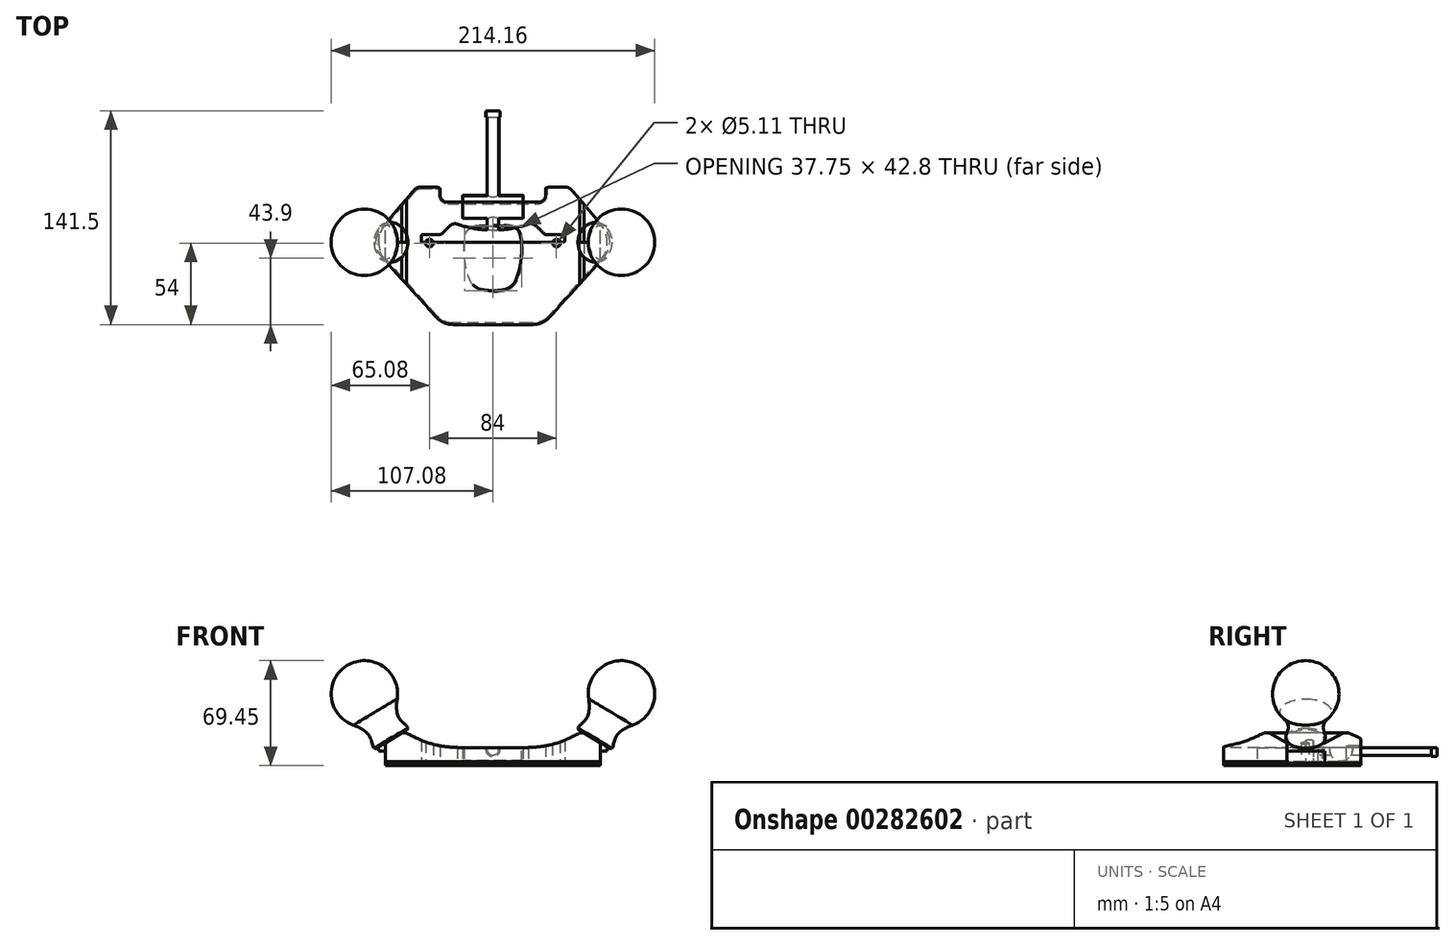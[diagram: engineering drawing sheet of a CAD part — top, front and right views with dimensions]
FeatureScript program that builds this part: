
annotation { "Feature Type Name" : "Feature", "Feature Type Description" : "" }
export const myFeature = defineFeature(function(context is Context, id is Id, definition is map)
    precondition{}
    {
        {
            var Q0;
            Q0=qCreatedBy(makeId("Top.planeOp"),FACE);
            var sketch = newSketch(context, id + "F0", { "sketchPlane" : qUnion([Q0])});
            skLineSegment(sketch, "E0", {"start": v(-47.5, 0) * mm, "end": v(47.5, 0) * mm});
            skPoint(sketch, "E1", {"position": v(0, 0) * mm});
            skLineSegment(sketch, "E2", {"start": v(47.5, 0) * mm, "end": v(47.5, 5) * mm});
            skLineSegment(sketch, "E3", {"start": v(47.5, 5) * mm, "end": v(35.5, 5) * mm});
            skFitSpline(sketch, "E4", {"points": [v(35.5, 5) * mm, v(23.5, 12) * mm], "startDerivative": vector(-8.93, 0) * mm, "endDerivative": vector(-15.16, -5.98) * mm});
            skFitSpline(sketch, "E5.MirrorCS", {"points": [v(-35.5, 5) * mm, v(-23.5, 12) * mm], "startDerivative": vector(8.93, 0) * mm, "endDerivative": vector(15.16, -5.98) * mm});
            skLineSegment(sketch, "E6.MirrorCS", {"start": v(-47.5, 5) * mm, "end": v(-35.5, 5) * mm});
            skLineSegment(sketch, "E7.MirrorCS", {"start": v(-47.5, 0) * mm, "end": v(-47.5, 5) * mm});
            skArc(sketch, "E8", {"start": v(-23.5, 12) * mm, "mid": v(0, 8) * mm, "end": v(23.5, 12) * mm});
            skPoint(sketch, "E9", {"position": v(0, 8) * mm});
            skSolve(sketch);
        }
        {
            var Q0;
            Q0=makeQuery(id+"F0.imprint","IMPRINT",FACE,{"disambiguationData":[TD([[makeQuery(id+"F0.imprint","IMPRINT",EDGE,{"derivedFrom":sQuery(id+"F0.wireOp",EDGE,"E0")}),1.0]])]});
            extrude(context, id + "F1", {"entities" : qUnion([Q0]), "depth" : 18.5 * mm});
        }
        {
            var Q0;
            Q0=makeQuery(id+"F1.opExtrude","SWEPT_FACE",FACE,{"disambiguationData":[OSD([sQuery(id+"F0.wireOp",EDGE,"E0")])]});
            var sketch = newSketch(context, id + "F2", { "sketchPlane" : qUnion([Q0])});
            skCircle(sketch, "E10", {"center": v(0, 9.25) * mm, "radius": 3.95 * mm});
            skCircle(sketch, "E11", {"center": v(0, 9.25) * mm, "radius": 4.75 * mm});
            skSolve(sketch);
        }
        {
            var Q0;
            Q0=makeQuery(id+"F2.imprint","IMPRINT",FACE,{"disambiguationData":[TD([[makeQuery(id+"F2.imprint","IMPRINT",EDGE,{"derivedFrom":sQuery(id+"F2.wireOp",EDGE,"E10")}),1.0]])]});
            extrude(context, id + "F3", {"entities" : qUnion([Q0]), "operationType" : NewBodyOperationType.ADD, "oppositeDirection" : true, "depth" : 87 * mm});
        }
        {
            var Q0;
            Q0=makeQuery(id+"F2.imprint","IMPRINT",FACE,{"disambiguationData":[TD([[makeQuery(id+"F2.imprint","IMPRINT",EDGE,{"derivedFrom":sQuery(id+"F2.wireOp",EDGE,"E10")}),-1.0]])]});
            var Q1;
            Q1=makeQuery(id+"F3.opExtrude","CAP_FACE",FACE,{"disambiguationData":[OSD([sQuery(id+"F2.wireOp",EDGE,"E10")])],"isStart":false});
            extrude(context, id + "F4", {"entities" : qUnion([Q0]), "operationType" : NewBodyOperationType.ADD, "endBound" : BoundingType.UP_TO_SURFACE, "oppositeDirection" : true, "endBoundEntityFace" : qUnion([Q1]), "depth" : 25 * mm, "hasSecondDirection" : true, "secondDirectionOppositeDirection" : true, "secondDirectionDepth" : 83 * mm});
        }
        {
            var Q0;
            Q0=qCreatedBy(makeId("Right.planeOp"),FACE);
            var sketch = newSketch(context, id + "F5", { "sketchPlane" : qUnion([Q0])});
            skPoint(sketch, "E12.0", {"position": v(0, 9.25) * mm});
            skCircle(sketch, "E13", {"center": v(23.3, 9.25) * mm, "radius": 7.65 * mm});
            skSolve(sketch);
        }
        {
            var Q0;
            Q0=makeQuery(id+"F5.imprint","IMPRINT",FACE,{"disambiguationData":[TD([[makeQuery(id+"F5.imprint","IMPRINT",EDGE,{"derivedFrom":sQuery(id+"F5.wireOp",EDGE,"E13")}),1.0]])]});
            extrude(context, id + "F6", {"entities" : qUnion([Q0]), "operationType" : NewBodyOperationType.ADD, "endBound" : BoundingType.SYMMETRIC, "depth" : 40 * mm});
        }
        {
            var Q0;
            Q0=makeQuery(id+"F1.opExtrude","SWEPT_EDGE",EDGE,{"disambiguationData":[OSD([sQuery(id+"F0.wireOp",EDGE,"E0"),sQuery(id+"F0.wireOp",EDGE,"E7.MirrorCS")])]});
            var Q1;
            Q1=makeQuery(id+"F1.opExtrude","SWEPT_EDGE",EDGE,{"disambiguationData":[OSD([sQuery(id+"F0.wireOp",EDGE,"E6.MirrorCS"),sQuery(id+"F0.wireOp",EDGE,"E7.MirrorCS")])]});
            var Q2;
            Q2=makeQuery(id+"F1.opExtrude","SWEPT_EDGE",EDGE,{"disambiguationData":[OSD([sQuery(id+"F0.wireOp",EDGE,"E0"),sQuery(id+"F0.wireOp",EDGE,"E2")])]});
            var Q3;
            Q3=makeQuery(id+"F1.opExtrude","SWEPT_EDGE",EDGE,{"disambiguationData":[OSD([sQuery(id+"F0.wireOp",EDGE,"E2"),sQuery(id+"F0.wireOp",EDGE,"E3")])]});
            var Q4;
            Q4=makeQuery(id+"F4.opExtrude","CAP_EDGE",EDGE,{"disambiguationData":[OSD([sQuery(id+"F2.wireOp",EDGE,"E11")])],"isStart":false});
            fillet(context, id + "F7", {"entities" : qUnion([Q0, Q1, Q2, Q3, Q4]), "radius" : 1 * mm, "tangentPropagation" : true, "allowEdgeOverflow" : false});
        }
        {
            var Q0;
            Q0=qCreatedBy(makeId("Top.planeOp"),FACE);
            var sketch = newSketch(context, id + "F8", { "sketchPlane" : qUnion([Q0])});
            skLineSegment(sketch, "E14", {"start": v(-25, -54.5) * mm, "end": v(25, -54.5) * mm});
            skPoint(sketch, "E15", {"position": v(0, -54.5) * mm});
            skLineSegment(sketch, "E16", {"start": v(37.5, -49.5) * mm, "end": v(71, -12.5) * mm});
            skLineSegment(sketch, "E17", {"start": v(71, -12.5) * mm, "end": v(71, 12.5) * mm});
            skPoint(sketch, "E18", {"position": v(71, 0) * mm});
            skFitSpline(sketch, "E19", {"points": [v(25, -54.5) * mm, v(37.5, -49.5) * mm], "startDerivative": vector(17.7, 0) * mm, "endDerivative": vector(9.15, 10.1) * mm});
            skLineSegment(sketch, "E20", {"start": v(71, 12.5) * mm, "end": v(53, 33.5) * mm});
            skLineSegment(sketch, "E21", {"start": v(47.5, 36.5) * mm, "end": v(38, 36.5) * mm});
            skPoint(sketch, "E22", {"position": v(0, 36.5) * mm});
            skLineSegment(sketch, "E23", {"start": v(-35, 26.5) * mm, "end": v(30, 26.5) * mm});
            skPoint(sketch, "E24", {"position": v(0, 26.5) * mm});
            skFitSpline(sketch, "E25", {"points": [v(47.5, 36.5) * mm, v(53, 33.5) * mm], "startDerivative": vector(8.49, 0) * mm, "endDerivative": vector(5.57, -6.5) * mm});
            skLineSegment(sketch, "E26", {"start": v(35, 31.5) * mm, "end": v(35, 35.69) * mm});
            skLineSegment(sketch, "E27", {"start": v(38, 36.5) * mm, "end": v(47.5, 36.5) * mm});
            skPoint(sketch, "E28.visualSharp", {"position": v(35, 26.5) * mm});
            skArc(sketch, "E28.filletArc", {"start": v(30, 26.5) * mm, "mid": v(33.54, 27.96) * mm, "end": v(35, 31.5) * mm});
            skFitSpline(sketch, "E29", {"points": [v(38, 36.5) * mm, v(33, 31.5) * mm], "startDerivative": vector(-10.17, 0) * mm, "endDerivative": vector(0, -8.22) * mm});
            skFitSpline(sketch, "E30", {"points": [v(38, 36.5) * mm, v(33, 31.5) * mm], "startDerivative": vector(-10.17, 0) * mm, "endDerivative": vector(0, -8.22) * mm, "construction": true});
            skLineSegment(sketch, "E31.trimOffspring", {"start": v(35, 36.5) * mm, "end": v(-47.5, 36.5) * mm, "construction": true});
            skFitSpline(sketch, "E32.MirrorCS", {"points": [v(-25, -54.5) * mm, v(-37.5, -49.5) * mm], "startDerivative": vector(-17.7, 0) * mm, "endDerivative": vector(-9.15, 10.1) * mm});
            skLineSegment(sketch, "E33.MirrorCS", {"start": v(-37.5, -49.5) * mm, "end": v(-71, -12.5) * mm});
            skLineSegment(sketch, "E34.MirrorCS", {"start": v(-71, -12.5) * mm, "end": v(-71, 12.5) * mm});
            skLineSegment(sketch, "E35.MirrorCS", {"start": v(-71, 12.5) * mm, "end": v(-53, 33.5) * mm});
            skFitSpline(sketch, "E36.MirrorCS", {"points": [v(-47.5, 36.5) * mm, v(-53, 33.5) * mm], "startDerivative": vector(-8.49, 0) * mm, "endDerivative": vector(-5.57, -6.5) * mm});
            skLineSegment(sketch, "E37.MirrorCS", {"start": v(-47.5, 36.5) * mm, "end": v(-38, 36.5) * mm, "construction": true});
            skLineSegment(sketch, "E38.MirrorCS", {"start": v(-47.5, 36.5) * mm, "end": v(-38, 36.5) * mm});
            skFitSpline(sketch, "E39.MirrorCS", {"points": [v(-38, 36.5) * mm, v(-33, 31.5) * mm], "startDerivative": vector(10.17, 0) * mm, "endDerivative": vector(0, -8.22) * mm});
            skLineSegment(sketch, "E40.MirrorCS", {"start": v(-35, 31.5) * mm, "end": v(-35, 35.69) * mm});
            skArc(sketch, "E41.MirrorCS", {"start": v(-30, 26.5) * mm, "mid": v(-33.54, 27.96) * mm, "end": v(-35, 31.5) * mm});
            skFitSpline(sketch, "E42", {"points": [v(0, -32) * mm, v(16, -23.23) * mm, v(18, 5.38) * mm, v(0, 10.8) * mm], "startDerivative": vector(99.32, 0) * mm, "endDerivative": vector(-122.6, 0) * mm});
            skFitSpline(sketch, "E43.MirrorCS", {"points": [v(0, -32) * mm, v(-16, -23.23) * mm, v(-18, 5.38) * mm, v(0, 10.8) * mm], "startDerivative": vector(-99.32, 0) * mm, "endDerivative": vector(122.6, 0) * mm});
            skPoint(sketch, "E44", {"position": v(42, -0.5) * mm});
            skArc(sketch, "E45", {"start": v(71, -12.5) * mm, "mid": v(75.62, 0) * mm, "end": v(71, 12.5) * mm});
            skArc(sketch, "E46.MirrorCS", {"start": v(-71, -12.5) * mm, "mid": v(-75.62, 0) * mm, "end": v(-71, 12.5) * mm});
            skPoint(sketch, "E47.MirrorP", {"position": v(-42, -0.5) * mm});
            skSolve(sketch);
        }
        {
            var Q0;
            Q0=makeQuery(id+"F8.imprint","IMPRINT",FACE,{"disambiguationData":[TD([[makeQuery(id+"F8.imprint","IMPRINT",EDGE,{"derivedFrom":sQuery(id+"F8.wireOp",EDGE,"E14")}),1.0]])]});
            var Q1;
            Q1=makeQuery(id+"F8.imprint","IMPRINT",FACE,{"disambiguationData":[TD([[makeQuery(id+"F8.imprint","IMPRINT",EDGE,{"derivedFrom":sQuery(id+"F8.wireOp",EDGE,"E17")}),-1.0]])]});
            var Q2;
            Q2=makeQuery(id+"F8.imprint","IMPRINT",FACE,{"disambiguationData":[TD([[makeQuery(id+"F8.imprint","IMPRINT",EDGE,{"derivedFrom":sQuery(id+"F8.wireOp",EDGE,"E34.MirrorCS")}),1.0]])]});
            extrude(context, id + "F9", {"entities" : qUnion([Q0, Q1, Q2]), "depth" : 20 * mm});
        }
        {
            var Q0;
            Q0=makeQuery(id+"F8.imprint","IMPRINT",FACE,{"disambiguationData":[TD([[makeQuery(id+"F8.imprint","IMPRINT",EDGE,{"derivedFrom":sQuery(id+"F8.wireOp",EDGE,"E34.MirrorCS")}),1.0]])]});
            var Q1;
            Q1=makeQuery(id+"F8.imprint","IMPRINT",FACE,{"disambiguationData":[TD([[makeQuery(id+"F8.imprint","IMPRINT",EDGE,{"derivedFrom":sQuery(id+"F8.wireOp",EDGE,"E17")}),-1.0]])]});
            extrude(context, id + "F10", {"entities" : qUnion([Q0, Q1]), "operationType" : NewBodyOperationType.REMOVE, "depth" : 8 * mm});
        }
        {
            var Q0;
            Q0=qCreatedBy(makeId("Front.planeOp"),FACE);
            var sketch = newSketch(context, id + "F11", { "sketchPlane" : qUnion([Q0])});
            skLineSegment(sketch, "E48", {"start": v(-20, 10.4) * mm, "end": v(20, 10.4) * mm});
            skPoint(sketch, "E49", {"position": v(0, 10.4) * mm});
            skFitSpline(sketch, "E50", {"points": [v(20, 10.4) * mm, v(57.32, 20) * mm], "startDerivative": vector(50.84, 0) * mm, "endDerivative": vector(35.71, 18.47) * mm});
            skLineSegment(sketch, "E51", {"start": v(75.62, 10.8) * mm, "end": v(60.31, 20) * mm});
            skLineSegment(sketch, "E52", {"start": v(0, 0) * mm, "end": v(75.62, 0) * mm});
            skPoint(sketch, "E53.0", {"position": v(75.62, 20) * mm});
            skLineSegment(sketch, "E54", {"start": v(75.62, 10.8) * mm, "end": v(75.62, 8) * mm});
            skLineSegment(sketch, "E55", {"start": v(75.62, 8) * mm, "end": v(75.62, 0) * mm});
            skLineSegment(sketch, "E56", {"start": v(57.32, 20) * mm, "end": v(60.31, 20) * mm});
            skFitSpline(sketch, "E57.MirrorCS", {"points": [v(-20, 10.4) * mm, v(-57.32, 20) * mm], "startDerivative": vector(-50.84, 0) * mm, "endDerivative": vector(-35.71, 18.47) * mm});
            skLineSegment(sketch, "E58.MirrorCS", {"start": v(-57.32, 20) * mm, "end": v(-60.31, 20) * mm});
            skLineSegment(sketch, "E59.MirrorCS", {"start": v(-75.62, 10.8) * mm, "end": v(-60.31, 20) * mm});
            skLineSegment(sketch, "E60.MirrorCS", {"start": v(-75.62, 10.8) * mm, "end": v(-75.62, 8) * mm});
            skLineSegment(sketch, "E61.MirrorCS", {"start": v(-75.62, 8) * mm, "end": v(-75.62, 0) * mm});
            skLineSegment(sketch, "E62.MirrorCS", {"start": v(0, 0) * mm, "end": v(-75.62, 0) * mm});
            skPoint(sketch, "E63", {"position": v(67.05, 15.95) * mm});
            skLineSegment(sketch, "E64", {"start": v(67.05, 15.95) * mm, "end": v(96.4, 64.8) * mm});
            skLineSegment(sketch, "E65", {"start": v(67.05, 15.95) * mm, "end": v(78.02, 9.36) * mm});
            skArc(sketch, "E66", {"start": v(73.75, 27.1) * mm, "mid": v(82.9, 24.06) * mm, "end": v(92.48, 25.23) * mm, "construction": true});
            skFitSpline(sketch, "E67", {"points": [v(92.48, 25.23) * mm, v(78.02, 9.36) * mm], "startDerivative": vector(-46.63, -16.14) * mm, "endDerivative": vector(-11.75, -8.8) * mm});
            skArc(sketch, "E68", {"start": v(92.48, 25.23) * mm, "mid": v(106.97, 43.78) * mm, "end": v(96.4, 64.8) * mm});
            skSolve(sketch);
        }
        {
            var Q0;
            {var subQ0=sQuery(id+"F11.wireOp",EDGE,"E58.MirrorCS");Q0=makeQuery(id+"F11.imprint","IMPRINT",FACE,{"disambiguationData":[TD([[makeQuery(id+"F11.imprint","IMPRINT",EDGE,{"derivedFrom":subQ0}),1.0]])]});}
            var Q1;
            {var subQ1=sQuery(id+"F11.wireOp",EDGE,"E48");Q1=makeQuery(id+"F11.imprint","IMPRINT",FACE,{"disambiguationData":[TD([[makeQuery(id+"F11.imprint","IMPRINT",EDGE,{"derivedFrom":subQ1}),-1.0]])]});}
            var Q2;
            Q2=makeQuery(id+"F11.imprint","IMPRINT",FACE,{"disambiguationData":[TD([[makeQuery(id+"F11.imprint","IMPRINT",EDGE,{"derivedFrom":sQuery(id+"F11.wireOp",EDGE,"E51")}),1.0]])]});
            extrude(context, id + "F12", {"entities" : qUnion([Q0, Q1, Q2]), "operationType" : NewBodyOperationType.INTERSECT, "endBound" : BoundingType.THROUGH_ALL, "oppositeDirection" : true, "depth" : 25 * mm, "hasSecondDirection" : true, "secondDirectionBound" : SecondDirectionBoundingType.THROUGH_ALL, "secondDirectionOppositeDirection" : false, "secondDirectionDepth" : 25 * mm});
        }
        {
            var Q0;
            {var subQ3=sQuery(id+"F11.wireOp",EDGE,"E64");Q0=makeQuery(id+"F11.imprint","IMPRINT",FACE,{"disambiguationData":[TD([[makeQuery(id+"F11.imprint","IMPRINT",EDGE,{"derivedFrom":subQ3}),-1.0]])]});}
            var Q1;
            Q1=sQuery(id+"F11.wireOp",EDGE,"E64");
            revolve(context, id + "F13", {"entities" : qUnion([Q0]), "axis" : qUnion([Q1]), "revolveType" : RevolveType.FULL});
        }
        {
            var Q0;
            Q0=makeQuery(id+"F13.opRevolve","SWEPT_EDGE",EDGE,{"disambiguationData":[OSD([sQuery(id+"F11.wireOp",EDGE,"E65"),sQuery(id+"F11.wireOp",EDGE,"E67")])]});
            chamfer(context, id + "F14", {"entities" : qUnion([Q0]), "width" : 1 * mm, "tangentPropagation" : true});
        }
        {
            var Q0;
            Q0=makeQuery(id+"F13.opRevolve","SWEPT_BODY",BODY,{"disambiguationData":[OSD([sQuery(id+"F11.wireOp",EDGE,"E64"),sQuery(id+"F11.wireOp",EDGE,"E65"),sQuery(id+"F11.wireOp",EDGE,"E67"),sQuery(id+"F11.wireOp",EDGE,"E68")])]});
            var Q1;
            Q1=qCreatedBy(makeId("Right.planeOp"),FACE);
            mirror(context, id + "F15", {"entities" : qUnion([Q0]), "mirrorPlane" : qUnion([Q1])});
        }
        {
            var Q0;
            Q0=sQuery(id+"F8.wireOp",VERTEX,"E47.MirrorP");
            var Q1;
            Q1=sQuery(id+"F8.wireOp",VERTEX,"E44");
            var Q2;
            Q2=makeQuery(id+"F9.opExtrude","SWEPT_BODY",BODY,{"disambiguationData":[OSD([sQuery(id+"F8.wireOp",EDGE,"E14"),sQuery(id+"F8.wireOp",EDGE,"E16"),sQuery(id+"F8.wireOp",EDGE,"E19"),sQuery(id+"F8.wireOp",EDGE,"E20"),sQuery(id+"F8.wireOp",EDGE,"E23"),sQuery(id+"F8.wireOp",EDGE,"E25"),sQuery(id+"F8.wireOp",EDGE,"E26"),sQuery(id+"F8.wireOp",EDGE,"E27"),sQuery(id+"F8.wireOp",EDGE,"E28.filletArc"),sQuery(id+"F8.wireOp",EDGE,"E29"),sQuery(id+"F8.wireOp",EDGE,"E32.MirrorCS"),sQuery(id+"F8.wireOp",EDGE,"E33.MirrorCS"),sQuery(id+"F8.wireOp",EDGE,"E35.MirrorCS"),sQuery(id+"F8.wireOp",EDGE,"E36.MirrorCS"),sQuery(id+"F8.wireOp",EDGE,"E38.MirrorCS"),sQuery(id+"F8.wireOp",EDGE,"E39.MirrorCS"),sQuery(id+"F8.wireOp",EDGE,"E40.MirrorCS"),sQuery(id+"F8.wireOp",EDGE,"E41.MirrorCS"),sQuery(id+"F8.wireOp",EDGE,"E42"),sQuery(id+"F8.wireOp",EDGE,"E43.MirrorCS"),sQuery(id+"F8.wireOp",EDGE,"E45"),sQuery(id+"F8.wireOp",EDGE,"E46.MirrorCS")])]});
            hole(context, id + "F16", {"style" : HoleStyle.SIMPLE, "endStyle" : HoleEndStyle.THROUGH, "oppositeDirection" : true, "standardTappedOrClearance" : lookupTablePath({ "standard" : "ANSI", "fit" : "Normal (ASME)", "size" : "#10", "type" : "Clearance" }), "standardBlindInLast" : lookupTablePath({ "fit" : "Free", "standard" : "ANSI", "size" : "#10", "type" : "Clearance" }), "holeDiameter" : 5.1 * mm, "tappedDepth" : 12 * mm, "tapClearance" : 3, "locations" : qUnion([Q0, Q1]), "scope" : qUnion([Q2])});
        }
        {
            var Q0;
            Q0=makeQuery(id+"F8.imprint","IMPRINT",FACE,{"disambiguationData":[TD([[makeQuery(id+"F8.imprint","IMPRINT",EDGE,{"derivedFrom":sQuery(id+"F8.wireOp",EDGE,"E14")}),1.0]])]});
            extrude(context, id + "F17", {"entities" : qUnion([Q0]), "oppositeDirection" : true, "depth" : 1.5 * mm});
        }
        {
            var Q0;
            Q0=makeQuery(id+"F9.opExtrude","CAP_EDGE",EDGE,{"disambiguationData":[OSD([sQuery(id+"F8.wireOp",EDGE,"E33.MirrorCS")])],"isStart":true});
            var Q1;
            Q1=makeQuery(id+"F9.opExtrude","CAP_EDGE",EDGE,{"disambiguationData":[OSD([sQuery(id+"F8.wireOp",EDGE,"E32.MirrorCS")])],"isStart":true});
            var Q2;
            Q2=makeQuery(id+"F10.boolean.opBoolean","COPY",EDGE,{"derivedFrom":makeQuery(id+"F10.opExtrude","CAP_EDGE",EDGE,{"disambiguationData":[OSD([sQuery(id+"F8.wireOp",EDGE,"E34.MirrorCS")])],"isStart":true})});
            var Q3;
            Q3=makeQuery(id+"F9.opExtrude","CAP_EDGE",EDGE,{"disambiguationData":[OSD([sQuery(id+"F8.wireOp",EDGE,"E35.MirrorCS")])],"isStart":true});
            var Q4;
            Q4=makeQuery(id+"F9.opExtrude","CAP_EDGE",EDGE,{"disambiguationData":[OSD([sQuery(id+"F8.wireOp",EDGE,"E40.MirrorCS")])],"isStart":true});
            var Q5;
            Q5=makeQuery(id+"F9.opExtrude","CAP_EDGE",EDGE,{"disambiguationData":[OSD([sQuery(id+"F8.wireOp",EDGE,"E27")])],"isStart":true});
            var Q6;
            Q6=makeQuery(id+"F10.boolean.opBoolean","COPY",EDGE,{"derivedFrom":makeQuery(id+"F10.opExtrude","CAP_EDGE",EDGE,{"disambiguationData":[OSD([sQuery(id+"F8.wireOp",EDGE,"E17")])],"isStart":true})});
            var Q7;
            Q7=makeQuery(id+"F9.opExtrude","CAP_EDGE",EDGE,{"disambiguationData":[OSD([sQuery(id+"F8.wireOp",EDGE,"E42")])],"isStart":true});
            chamfer(context, id + "F18", {"entities" : qUnion([Q0, Q1, Q2, Q3, Q4, Q5, Q6, Q7]), "width" : 1 * mm, "tangentPropagation" : true});
        }
        {
            var Q0;
            Q0=makeQuery(id+"F1.opExtrude","CAP_FACE",FACE,{"disambiguationData":[OSD([sQuery(id+"F0.wireOp",EDGE,"E0"),sQuery(id+"F0.wireOp",EDGE,"E2"),sQuery(id+"F0.wireOp",EDGE,"E3"),sQuery(id+"F0.wireOp",EDGE,"E4"),sQuery(id+"F0.wireOp",EDGE,"E5.MirrorCS"),sQuery(id+"F0.wireOp",EDGE,"E6.MirrorCS"),sQuery(id+"F0.wireOp",EDGE,"E7.MirrorCS"),sQuery(id+"F0.wireOp",EDGE,"E8")])],"isStart":true});
            extrude(context, id + "F19", {"entities" : qUnion([Q0]), "depth" : 1.5 * mm});
        }
    });
